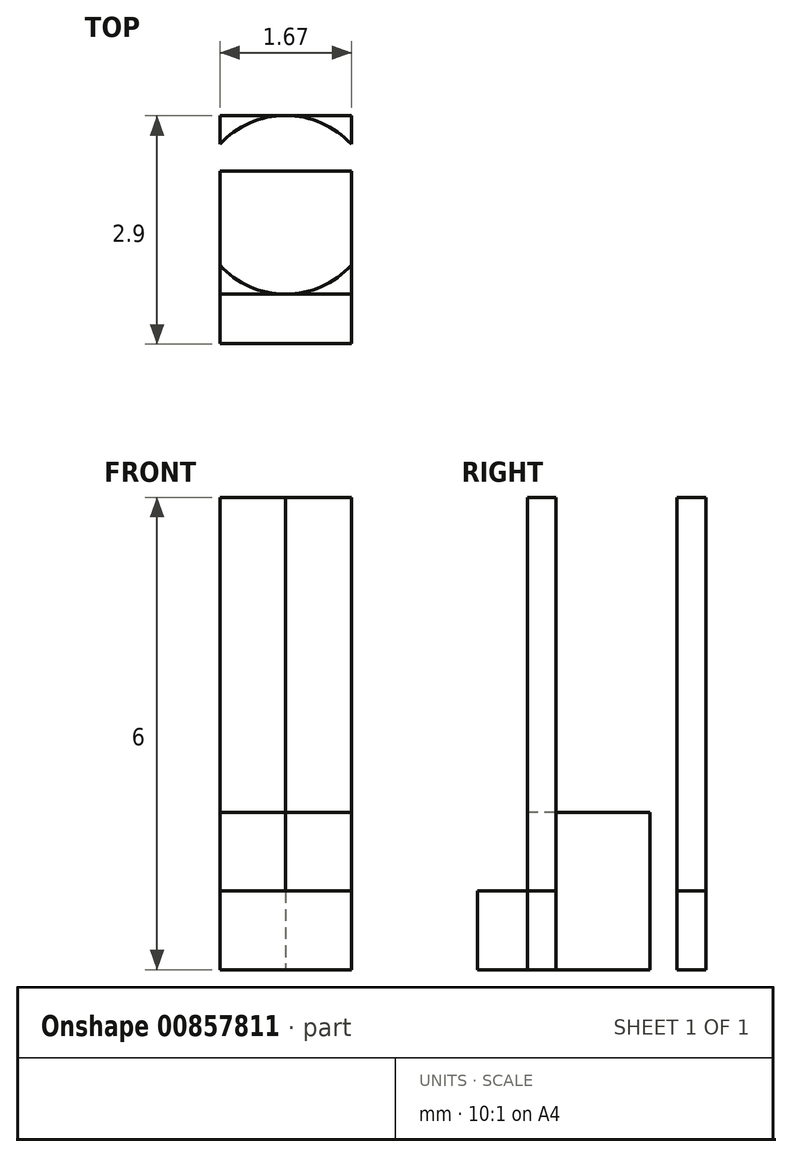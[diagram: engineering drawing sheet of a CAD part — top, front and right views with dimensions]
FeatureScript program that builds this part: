
annotation { "Feature Type Name" : "Feature", "Feature Type Description" : "" }
export const myFeature = defineFeature(function(context is Context, id is Id, definition is map)
    precondition{}
    {
        {
            var Q0;
            Q0=qCreatedBy(makeId("Top.planeOp"),FACE);
            var sketch = newSketch(context, id + "F0", { "sketchPlane" : qUnion([Q0])});
            skLineSegment(sketch, "E0.bottom", {"start": v(-0.55, 1.76) * mm, "end": v(1.12, 1.76) * mm});
            skLineSegment(sketch, "E0.top", {"start": v(-0.55, -1.14) * mm, "end": v(1.12, -1.14) * mm});
            skLineSegment(sketch, "E0.left", {"start": v(-0.55, 1.76) * mm, "end": v(-0.55, -1.14) * mm});
            skLineSegment(sketch, "E0.right", {"start": v(1.12, 1.76) * mm, "end": v(1.12, -1.14) * mm});
            skPoint(sketch, "E1.third.point", {"position": v(0.28, 1.76) * mm});
            skPoint(sketch, "E2", {"position": v(-0.55, -0.5) * mm});
            skLineSegment(sketch, "E3", {"start": v(-0.55, -0.5) * mm, "end": v(1.12, -0.5) * mm});
            skLineSegment(sketch, "E4", {"start": v(0.28, 1.76) * mm, "end": v(0.28, -0.5) * mm});
            skPoint(sketch, "E5", {"position": v(-0.85, 0.63) * mm});
            skCircle(sketch, "E6", {"center": v(0.28, 0.63) * mm, "radius": 1.14 * mm});
            skLineSegment(sketch, "E7.0", {"start": v(0.28, -4.37) * mm, "end": v(2.25, -4.37) * mm});
            skCircle(sketch, "E8.0", {"center": v(0.28, 0.63) * mm, "radius": 0.64 * mm});
            skPoint(sketch, "E9", {"position": v(-0.85, 1.05) * mm});
            skLineSegment(sketch, "E10", {"start": v(0.28, 0.63) * mm, "end": v(-0.85, 0.63) * mm});
            skLineSegment(sketch, "E11", {"start": v(0.28, 0.63) * mm, "end": v(1.42, 0.63) * mm});
            skPoint(sketch, "E12.MirrorP", {"position": v(-0.85, 0.2) * mm});
            skPoint(sketch, "E13.MirrorP", {"position": v(1.42, 1.05) * mm});
            skPoint(sketch, "E14.MirrorP", {"position": v(1.42, 0.2) * mm});
            skLineSegment(sketch, "E15", {"start": v(-0.85, 1.05) * mm, "end": v(1.42, 1.05) * mm});
            skLineSegment(sketch, "E16", {"start": v(1.42, 0.2) * mm, "end": v(-0.85, 0.2) * mm});
            skSolve(sketch);
        }
        {
            var Q0;
            {var subQ1=sQuery(id+"F0.wireOp",EDGE,"E0.top");Q0=makeQuery(id+"F0.imprint","IMPRINT",FACE,{"disambiguationData":[TD([[makeQuery(id+"F0.imprint","IMPRINT",EDGE,{"derivedFrom":subQ1}),1.0]])]});}
            var Q1;
            {var subQ0=sQuery(id+"F0.wireOp",EDGE,"E3");var subQ1=sQuery(id+"F0.wireOp",EDGE,"E0.left");var subQ2=makeQuery(id+"F0.imprint","INTERSECT",VERTEX,{"derivedFrom":[subQ1,subQ0]});Q1=makeQuery(id+"F0.imprint","IMPRINT",FACE,{"disambiguationData":[TD([[makeQuery(id+"F0.imprint","IMPRINT",EDGE,{"disambiguationData":[TD([[subQ2,1.0]])],"derivedFrom":subQ1}),1.0]])]});}
            var Q2;
            {var subQ0=sQuery(id+"F0.wireOp",EDGE,"E3");var subQ1=sQuery(id+"F0.wireOp",EDGE,"E0.right");var subQ2=makeQuery(id+"F0.imprint","INTERSECT",VERTEX,{"derivedFrom":[subQ1,subQ0]});Q2=makeQuery(id+"F0.imprint","IMPRINT",FACE,{"disambiguationData":[TD([[makeQuery(id+"F0.imprint","IMPRINT",EDGE,{"disambiguationData":[TD([[subQ2,1.0]])],"derivedFrom":subQ1}),-1.0]])]});}
            var Q3;
            {var subQ0=sQuery(id+"F0.wireOp",EDGE,"E0.right");var subQ1=sQuery(id+"F0.wireOp",EDGE,"E0.bottom");var subQ2=makeQuery(id+"F0.imprint","INTERSECT",VERTEX,{"derivedFrom":[subQ1,subQ0]});Q3=makeQuery(id+"F0.imprint","IMPRINT",FACE,{"disambiguationData":[TD([[makeQuery(id+"F0.imprint","IMPRINT",EDGE,{"disambiguationData":[TD([[subQ2,-1.0]])],"derivedFrom":subQ0}),-1.0]])]});}
            var Q4;
            {var subQ0=sQuery(id+"F0.wireOp",EDGE,"E0.left");var subQ1=sQuery(id+"F0.wireOp",EDGE,"E0.bottom");var subQ2=makeQuery(id+"F0.imprint","INTERSECT",VERTEX,{"derivedFrom":[subQ1,subQ0]});Q4=makeQuery(id+"F0.imprint","IMPRINT",FACE,{"disambiguationData":[TD([[makeQuery(id+"F0.imprint","IMPRINT",EDGE,{"disambiguationData":[TD([[subQ2,-1.0]])],"derivedFrom":subQ0}),1.0]])]});}
            extrude(context, id + "F1", {"entities" : qUnion([Q0, Q1, Q2, Q3, Q4]), "depth" : 1 * mm, "offsetDistance" : 25 * mm});
        }
        {
            var Q0;
            {var subQ0=sQuery(id+"F0.wireOp",EDGE,"E10");var subQ5=sQuery(id+"F0.wireOp",EDGE,"E8.0");var subQ6=makeQuery(id+"F0.imprint","INTERSECT",VERTEX,{"derivedFrom":[subQ5,subQ0]});Q0=makeQuery(id+"F0.imprint","IMPRINT",FACE,{"disambiguationData":[TD([[makeQuery(id+"F0.imprint","IMPRINT",EDGE,{"disambiguationData":[TD([[subQ6,-1.0]])],"derivedFrom":subQ5}),1.0]])]});}
            var Q1;
            {var subQ0=sQuery(id+"F0.wireOp",EDGE,"E10");var subQ1=sQuery(id+"F0.wireOp",EDGE,"E0.left");var subQ2=makeQuery(id+"F0.imprint","INTERSECT",VERTEX,{"derivedFrom":[subQ1,subQ0]});Q1=makeQuery(id+"F0.imprint","IMPRINT",FACE,{"disambiguationData":[TD([[makeQuery(id+"F0.imprint","IMPRINT",EDGE,{"disambiguationData":[TD([[subQ2,-1.0]])],"derivedFrom":subQ1}),1.0]])]});}
            var Q2;
            {var subQ0=sQuery(id+"F0.wireOp",EDGE,"E15");var subQ1=sQuery(id+"F0.wireOp",EDGE,"E0.left");var subQ2=makeQuery(id+"F0.imprint","INTERSECT",VERTEX,{"derivedFrom":[subQ1,subQ0]});Q2=makeQuery(id+"F0.imprint","IMPRINT",FACE,{"disambiguationData":[TD([[makeQuery(id+"F0.imprint","IMPRINT",EDGE,{"disambiguationData":[TD([[subQ2,-1.0]])],"derivedFrom":subQ1}),1.0]])]});}
            var Q3;
            {var subQ3=sQuery(id+"F0.wireOp",EDGE,"E15");var subQ5=sQuery(id+"F0.wireOp",EDGE,"E8.0");var subQ6=makeQuery(id+"F0.imprint","INTERSECT",VERTEX,{"disambiguationData":[OD(1.0)],"derivedFrom":[subQ5,subQ3]});Q3=makeQuery(id+"F0.imprint","IMPRINT",FACE,{"disambiguationData":[TD([[makeQuery(id+"F0.imprint","IMPRINT",EDGE,{"disambiguationData":[TD([[subQ6,-1.0]])],"derivedFrom":subQ5}),1.0]])]});}
            var Q4;
            {var subQ3=sQuery(id+"F0.wireOp",EDGE,"E15");var subQ5=sQuery(id+"F0.wireOp",EDGE,"E8.0");var subQ6=makeQuery(id+"F0.imprint","INTERSECT",VERTEX,{"disambiguationData":[OD(0.0)],"derivedFrom":[subQ5,subQ3]});Q4=makeQuery(id+"F0.imprint","IMPRINT",FACE,{"disambiguationData":[TD([[makeQuery(id+"F0.imprint","IMPRINT",EDGE,{"disambiguationData":[TD([[subQ6,1.0]])],"derivedFrom":subQ5}),1.0]])]});}
            var Q5;
            {var subQ0=sQuery(id+"F0.wireOp",EDGE,"E15");var subQ1=sQuery(id+"F0.wireOp",EDGE,"E0.right");var subQ2=makeQuery(id+"F0.imprint","INTERSECT",VERTEX,{"derivedFrom":[subQ1,subQ0]});Q5=makeQuery(id+"F0.imprint","IMPRINT",FACE,{"disambiguationData":[TD([[makeQuery(id+"F0.imprint","IMPRINT",EDGE,{"disambiguationData":[TD([[subQ2,-1.0]])],"derivedFrom":subQ1}),-1.0]])]});}
            var Q6;
            {var subQ0=sQuery(id+"F0.wireOp",EDGE,"E11");var subQ1=sQuery(id+"F0.wireOp",EDGE,"E0.right");var subQ2=makeQuery(id+"F0.imprint","INTERSECT",VERTEX,{"derivedFrom":[subQ1,subQ0]});Q6=makeQuery(id+"F0.imprint","IMPRINT",FACE,{"disambiguationData":[TD([[makeQuery(id+"F0.imprint","IMPRINT",EDGE,{"disambiguationData":[TD([[subQ2,-1.0]])],"derivedFrom":subQ1}),-1.0]])]});}
            var Q7;
            {var subQ0=sQuery(id+"F0.wireOp",EDGE,"E16");var subQ1=sQuery(id+"F0.wireOp",EDGE,"E4");var subQ2=makeQuery(id+"F0.imprint","INTERSECT",VERTEX,{"derivedFrom":[subQ1,subQ0]});Q7=makeQuery(id+"F0.imprint","IMPRINT",FACE,{"disambiguationData":[TD([[makeQuery(id+"F0.imprint","IMPRINT",EDGE,{"disambiguationData":[TD([[subQ2,-1.0]])],"derivedFrom":subQ1}),1.0]])]});}
            var Q8;
            {var subQ0=sQuery(id+"F0.wireOp",EDGE,"E16");var subQ1=sQuery(id+"F0.wireOp",EDGE,"E4");var subQ2=makeQuery(id+"F0.imprint","INTERSECT",VERTEX,{"derivedFrom":[subQ1,subQ0]});Q8=makeQuery(id+"F0.imprint","IMPRINT",FACE,{"disambiguationData":[TD([[makeQuery(id+"F0.imprint","IMPRINT",EDGE,{"disambiguationData":[TD([[subQ2,-1.0]])],"derivedFrom":subQ1}),-1.0]])]});}
            var Q9;
            {var subQ0=sQuery(id+"F0.wireOp",EDGE,"E11");var subQ5=sQuery(id+"F0.wireOp",EDGE,"E8.0");var subQ6=makeQuery(id+"F0.imprint","INTERSECT",VERTEX,{"derivedFrom":[subQ5,subQ0]});Q9=makeQuery(id+"F0.imprint","IMPRINT",FACE,{"disambiguationData":[TD([[makeQuery(id+"F0.imprint","IMPRINT",EDGE,{"disambiguationData":[TD([[subQ6,1.0]])],"derivedFrom":subQ5}),1.0]])]});}
            var Q10;
            {var subQ0=sQuery(id+"F0.wireOp",EDGE,"E8.0");var subQ1=sQuery(id+"F0.wireOp",EDGE,"E4");var subQ2=makeQuery(id+"F0.imprint","INTERSECT",VERTEX,{"disambiguationData":[OD(0.0)],"derivedFrom":[subQ1,subQ0]});Q10=makeQuery(id+"F0.imprint","IMPRINT",FACE,{"disambiguationData":[TD([[makeQuery(id+"F0.imprint","IMPRINT",EDGE,{"disambiguationData":[TD([[subQ2,-1.0]])],"derivedFrom":subQ1}),1.0]])]});}
            var Q11;
            {var subQ0=sQuery(id+"F0.wireOp",EDGE,"E8.0");var subQ1=sQuery(id+"F0.wireOp",EDGE,"E4");var subQ2=makeQuery(id+"F0.imprint","INTERSECT",VERTEX,{"disambiguationData":[OD(0.0)],"derivedFrom":[subQ1,subQ0]});Q11=makeQuery(id+"F0.imprint","IMPRINT",FACE,{"disambiguationData":[TD([[makeQuery(id+"F0.imprint","IMPRINT",EDGE,{"disambiguationData":[TD([[subQ2,-1.0]])],"derivedFrom":subQ1}),-1.0]])]});}
            extrude(context, id + "F2", {"entities" : qUnion([Q0, Q1, Q2, Q3, Q4, Q5, Q6, Q7, Q8, Q9, Q10, Q11]), "depth" : 2 * mm, "offsetDistance" : 25 * mm});
        }
        {
            var Q0;
            {var subQ0=sQuery(id+"F0.wireOp",EDGE,"E6");var subQ3=sQuery(id+"F0.wireOp",EDGE,"E0.left");var subQ4=makeQuery(id+"F0.imprint","INTERSECT",VERTEX,{"disambiguationData":[OD(0.0)],"derivedFrom":[subQ3,subQ0]});Q0=makeQuery(id+"F0.imprint","IMPRINT",FACE,{"disambiguationData":[TD([[makeQuery(id+"F0.imprint","IMPRINT",EDGE,{"disambiguationData":[TD([[subQ4,-1.0]])],"derivedFrom":subQ3}),1.0]])]});}
            var Q1;
            {var subQ5=sQuery(id+"F0.wireOp",EDGE,"E6");var subQ7=sQuery(id+"F0.wireOp",EDGE,"E0.right");var subQ8=makeQuery(id+"F0.imprint","INTERSECT",VERTEX,{"disambiguationData":[OD(0.0)],"derivedFrom":[subQ7,subQ5]});Q1=makeQuery(id+"F0.imprint","IMPRINT",FACE,{"disambiguationData":[TD([[makeQuery(id+"F0.imprint","IMPRINT",EDGE,{"disambiguationData":[TD([[subQ8,-1.0]])],"derivedFrom":subQ7}),-1.0]])]});}
            var Q2;
            {var subQ0=sQuery(id+"F0.wireOp",EDGE,"E6");var subQ3=sQuery(id+"F0.wireOp",EDGE,"E0.left");var subQ4=makeQuery(id+"F0.imprint","INTERSECT",VERTEX,{"disambiguationData":[OD(1.0)],"derivedFrom":[subQ3,subQ0]});Q2=makeQuery(id+"F0.imprint","IMPRINT",FACE,{"disambiguationData":[TD([[makeQuery(id+"F0.imprint","IMPRINT",EDGE,{"disambiguationData":[TD([[subQ4,1.0]])],"derivedFrom":subQ3}),1.0]])]});}
            var Q3;
            {var subQ5=sQuery(id+"F0.wireOp",EDGE,"E6");var subQ7=sQuery(id+"F0.wireOp",EDGE,"E0.right");var subQ8=makeQuery(id+"F0.imprint","INTERSECT",VERTEX,{"disambiguationData":[OD(1.0)],"derivedFrom":[subQ7,subQ5]});Q3=makeQuery(id+"F0.imprint","IMPRINT",FACE,{"disambiguationData":[TD([[makeQuery(id+"F0.imprint","IMPRINT",EDGE,{"disambiguationData":[TD([[subQ8,1.0]])],"derivedFrom":subQ7}),-1.0]])]});}
            extrude(context, id + "F3", {"entities" : qUnion([Q0, Q1, Q2, Q3]), "depth" : 6 * mm, "offsetDistance" : 25 * mm});
        }
    });
